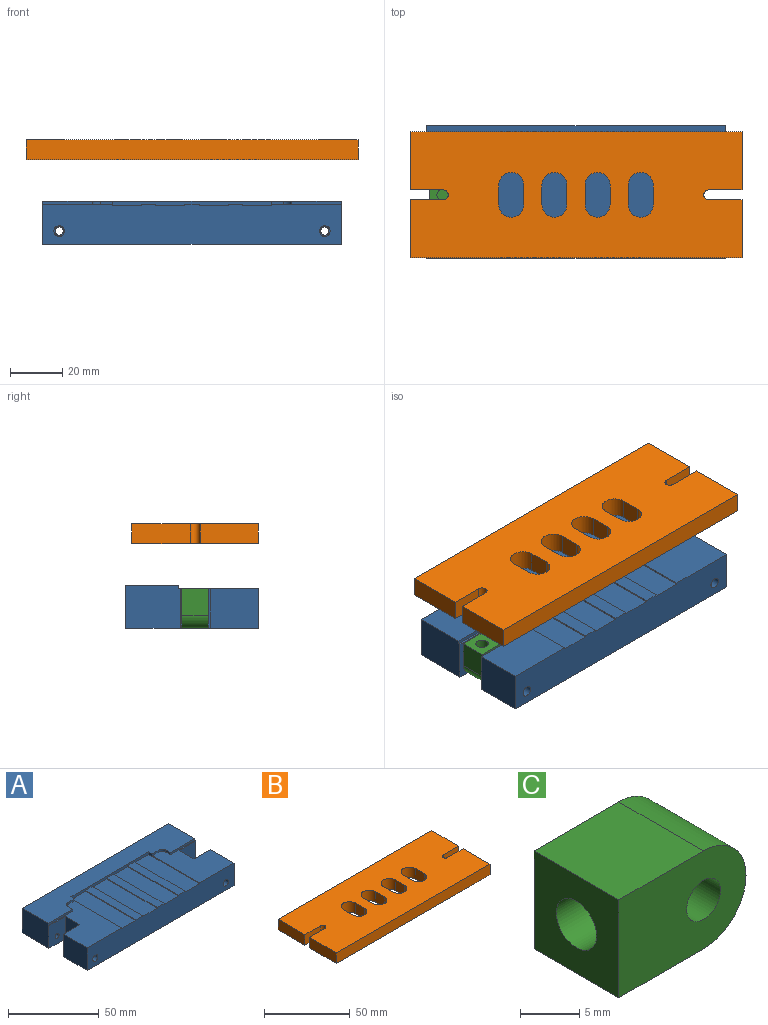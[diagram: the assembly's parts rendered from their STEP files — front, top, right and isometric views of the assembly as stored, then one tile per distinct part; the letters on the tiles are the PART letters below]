
ASSEMBLY  parts=3 mates=2
PART A: 44 faces, bbox 114.3x50.8x16.5 mm
  f0: plane 20.96x16.51mm, normal (1,0,0), area 345.2mm2, adj f1,f23,f24,f25,f30,f39
  f1: plane 36.83x26.82mm, normal (0,0,1), area 719.6mm2, adj f0,f17,f20,f22,f30,f31,f32,f33
  f2: plane 20.96x16.51mm, normal (-1,0,0), area 345.2mm2, adj f3,f23,f24,f25,f26,f34
  f3: plane 36.83x26.82mm, normal (0,0,1), area 719.6mm2, adj f2,f9,f21,f22,f26,f27,f28,f29
  f4: plane 60.66x1.78mm, normal (0,-1,0), area 99.6mm2, adj f5,f6,f7,f8,f9,f10,f11,f12
  f5: plane 39.5x5.39mm, normal (0,0,1), area 212.7mm2, adj f4,f14,f18,f22
  f6: plane 39.5x5.38mm, normal (0,0,1), area 212.7mm2, adj f4,f11,f15,f22
  f7: plane 39.5x5.39mm, normal (0,0,1), area 212.7mm2, adj f4,f8,f12,f22
  f8: plane 39.5x0.51mm, normal (-1,0,0), area 20.1mm2, adj f4,f7,f10,f22
  f9: plane 39.5x1.78mm, normal (1,0,0), area 23.5mm2, adj f3,f4,f10,f22,f24,f29
  f10: plane 39.5x11.13mm, normal (0,0,1), area 439.4mm2, adj f4,f8,f9,f22
  f11: plane 39.5x0.51mm, normal (-1,0,0), area 20.1mm2, adj f4,f6,f13,f22
  f12: plane 39.5x0.51mm, normal (1,0,0), area 20.1mm2, adj f4,f7,f13,f22
  f13: plane 39.5x11.13mm, normal (0,0,1), area 439.4mm2, adj f4,f11,f12,f22
  f14: plane 39.5x0.51mm, normal (-1,0,0), area 20.1mm2, adj f4,f5,f16,f22
  f15: plane 39.5x0.51mm, normal (1,0,0), area 20.1mm2, adj f4,f6,f16,f22
  f16: plane 39.5x11.13mm, normal (0,0,1), area 439.4mm2, adj f4,f14,f15,f22
  f17: plane 39.5x1.78mm, normal (-1,0,0), area 23.5mm2, adj f1,f4,f19,f22,f24,f31
  f18: plane 39.5x0.51mm, normal (1,0,0), area 20.1mm2, adj f4,f5,f19,f22
  f19: plane 39.5x11.13mm, normal (0,0,1), area 439.4mm2, adj f4,f17,f18,f22
  f20: plane 18.42x15.24mm, normal (1,0,0), area 280.6mm2, adj f1,f22,f23,f40
  f21: plane 18.42x15.24mm, normal (-1,0,0), area 280.6mm2, adj f3,f22,f23,f35
  f22: plane 114.3x15.24mm, normal (0,-1,0), area 1693.4mm2, adj f1,f3,f5,f6,f7,f8,f9,f10
  f23: plane 114.3x50.8mm, normal (0,0,-1), area 5516.1mm2, adj f0,f2,f20,f21,f22,f25,f34,f35
  f24: plane 114.3x20.32mm, normal (0,0,1), area 1681.3mm2, adj f0,f2,f4,f9,f17,f25,f26,f27
  f25: plane 114.3x16.51mm, normal (0,1,0), area 1871.3mm2, adj f0,f2,f23,f24,f38,f43
  f26: plane 19.05x1.27mm, normal (0,-1,0), area 24.2mm2, adj f2,f3,f24,f27
  f27: plane 3.18x1.27mm, normal (1,0,0), area 4mm2, adj f3,f24,f26,f28
  f28: cylinder r=3.17mm len=3.18mm, axis (0,0,-1), area 6.3mm2, adj f3,f24,f27,f29
  f29: plane 4.6x1.27mm, normal (0,-1,0), area 5.8mm2, adj f3,f9,f24,f28
  f30: plane 19.05x1.27mm, normal (0,-1,0), area 24.2mm2, adj f0,f1,f24,f33
  f31: plane 4.6x1.27mm, normal (0,-1,0), area 5.8mm2, adj f1,f17,f24,f32
  f32: cylinder r=3.17mm len=3.18mm, axis (0,0,-1), area 6.3mm2, adj f1,f24,f31,f33
  f33: plane 3.18x1.27mm, normal (-1,0,0), area 4mm2, adj f1,f24,f30,f32
  f34: plane 15.24x12.7mm, normal (0,-1,0), area 185.6mm2, adj f2,f3,f23,f36,f38
  f35: plane 15.24x12.7mm, normal (0,1,0), area 180.6mm2, adj f3,f21,f23,f36,f37
  f36: plane 15.24x11.43mm, normal (-1,0,0), area 174.2mm2, adj f3,f23,f34,f35
  f37: cylinder r=2.03mm len=18.42mm, axis (0,-1,0), area 235.1mm2, adj f22,f35
  f38: cylinder r=1.59mm len=20.96mm, axis (0,-1,0), area 209mm2, adj f25,f34
  f39: plane 15.24x12.7mm, normal (0,-1,0), area 185.6mm2, adj f0,f1,f23,f41,f43
  f40: plane 15.24x12.7mm, normal (0,1,0), area 180.6mm2, adj f1,f20,f23,f41,f42
  f41: plane 15.24x11.43mm, normal (1,0,0), area 174.2mm2, adj f1,f23,f39,f40
  f42: cylinder r=2.03mm len=18.42mm, axis (0,-1,0), area 235.1mm2, adj f22,f40
  f43: cylinder r=1.59mm len=20.96mm, axis (0,-1,0), area 209mm2, adj f25,f39
PART B: 30 faces, bbox 127x48.3x7.6 mm
  f0: plane 22.23x7.62mm, normal (1,0,0), area 169.4mm2, adj f1,f6,f7,f27
  f1: plane 127x48.26mm, normal (0,0,1), area 5445.5mm2, adj f0,f2,f3,f4,f5,f6,f8,f9
  f2: plane 22.23x7.62mm, normal (-1,0,0), area 169.4mm2, adj f1,f6,f7,f24
  f3: plane 22.23x7.62mm, normal (1,0,0), area 169.4mm2, adj f1,f4,f7,f28
  f4: plane 127x7.62mm, normal (0,1,0), area 967.7mm2, adj f1,f3,f5,f7
  f5: plane 22.23x7.62mm, normal (-1,0,0), area 169.4mm2, adj f1,f4,f7,f26
  f6: plane 127x7.62mm, normal (0,-1,0), area 967.7mm2, adj f0,f1,f2,f7
  f7: plane 127x48.26mm, normal (0,0,-1), area 5445.5mm2, adj f0,f2,f3,f4,f5,f6,f8,f9
  f8: cylinder r=4.76mm len=9.53mm, axis (0,0,-1), area 114mm2, adj f1,f7,f9,f10
  f9: plane 7.62x7.62mm, normal (1,0,0), area 58.1mm2, adj f1,f7,f8,f11
  f10: plane 7.62x7.62mm, normal (-1,0,0), area 58.1mm2, adj f1,f7,f8,f11
  f11: cylinder r=4.76mm len=9.53mm, axis (0,0,-1), area 114mm2, adj f1,f7,f9,f10
  f12: cylinder r=4.76mm len=9.53mm, axis (0,0,-1), area 114mm2, adj f1,f7,f13,f14
  f13: plane 7.62x7.62mm, normal (1,0,0), area 58.1mm2, adj f1,f7,f12,f15
  f14: plane 7.62x7.62mm, normal (-1,0,0), area 58.1mm2, adj f1,f7,f12,f15
  f15: cylinder r=4.76mm len=9.53mm, axis (0,0,-1), area 114mm2, adj f1,f7,f13,f14
  f16: cylinder r=4.76mm len=9.53mm, axis (0,0,-1), area 114mm2, adj f1,f7,f17,f18
  f17: plane 7.62x7.62mm, normal (1,0,0), area 58.1mm2, adj f1,f7,f16,f19
  f18: plane 7.62x7.62mm, normal (-1,0,0), area 58.1mm2, adj f1,f7,f16,f19
  f19: cylinder r=4.76mm len=9.53mm, axis (0,0,-1), area 114mm2, adj f1,f7,f17,f18
  f20: cylinder r=4.76mm len=9.53mm, axis (0,0,-1), area 114mm2, adj f1,f7,f21,f22
  f21: plane 7.62x7.62mm, normal (1,0,0), area 58.1mm2, adj f1,f7,f20,f23
  f22: plane 7.62x7.62mm, normal (-1,0,0), area 58.1mm2, adj f1,f7,f20,f23
  f23: cylinder r=4.76mm len=9.53mm, axis (0,0,-1), area 114mm2, adj f1,f7,f21,f22
  f24: plane 12.7x7.62mm, normal (0,1,0), area 96.8mm2, adj f1,f2,f7,f25
  f25: cylinder r=1.91mm len=7.62mm, axis (0,0,1), area 45.6mm2, adj f1,f7,f24,f26
  f26: plane 12.7x7.62mm, normal (0,-1,0), area 96.8mm2, adj f1,f5,f7,f25
  f27: plane 12.7x7.62mm, normal (0,1,0), area 96.8mm2, adj f0,f1,f7,f29
  f28: plane 12.7x7.62mm, normal (0,-1,0), area 96.8mm2, adj f1,f3,f7,f29
  f29: cylinder r=1.91mm len=7.62mm, axis (0,0,1), area 45.6mm2, adj f1,f7,f27,f28
PART C: 9 faces, bbox 15.2x10.2x10.2 mm
  f0: plane 10.16x10.16mm, normal (0,0,-1), area 103.2mm2, adj f1,f3,f5,f6
  f1: cylinder r=5.08mm len=10.16mm, axis (0,1,0), area 162.1mm2, adj f0,f2,f5,f6
  f2: plane 10.16x10.16mm, normal (0,0,1), area 103.2mm2, adj f1,f3,f5,f6
  f3: plane 10.16x10.16mm, normal (-1,0,0), area 84.9mm2, adj f0,f2,f5,f6,f7
  f4: cylinder r=2.03mm len=10.16mm, axis (0,1,0), area 129.7mm2, adj f5,f6
  f5: plane 15.24x10.16mm, normal (0,-1,0), area 130.8mm2, adj f0,f1,f2,f3,f4
  f6: plane 15.24x10.16mm, normal (0,1,0), area 130.8mm2, adj f0,f1,f2,f3,f4
  f7: cylinder r=2.41mm len=5.08mm, axis (-1,0,0), area 77mm2, adj f3,f8
  f8: plane 4.83x4.83mm, normal (-1,0,0), area 18.3mm2, adj f7
PLACE A t=(0.96,1.8,0)mm fixed
PLACE B t=(0.96,1.91,17.2)mm
PLACE C rot(axis=(0.71,0,-0.71),180deg) t=(-60,1.91,-60.96)mm
MATE slider C.f1 <-> A.f37  axis (0,-1,0) through (-49.84,-3.17,-10.16)mm
MATE slider C.f7 <-> B.f25  axis (0,0,1) through (-49.84,1.91,0)mm
